# Revit family: Workstations-Multi_Level-Teknion-B_ASP_Secondary_Desk_for_Height_Adjustable_Peninsula-R2018
name_source: partatom
category: Furniture
revit_build: Autodesk Revit 2018 (Build: 20190510_1515(x64)
units: mm (PartAtom-declared; Revit-internal decimal feet)

## family parameters
Always vertical = Yes
Cut with Voids When Loaded = No
OmniClass Number = 23.40.20.00
OmniClass Title = General Furniture and Specialties
Room Calculation Point = No
Shared = Yes
Work Plane-Based = No

## types (5) — shared parameters
Assembly Code = E2020200
Manufacturer = Teknion
Manufacturer Fax = 416.661.4586
Part Number = B_ASP
Product Documentation Link = https://www.teknion.com
Product Line = Expansion Casegoods
Product Page URL = https://www.teknion.com
Series = Expansion Casegoods
Sustainability Data = https://www.teknion.com
URL = www.teknion.com
Unit Weight URL = http://www.teknion.com
Warranty = http://www.teknion.com

## per-type parameters (varying)
| type | Description | Height Adjustable Peninsula Depth | Model |
| 35" Height-Adjustable Peninsula Depth | Secondary Desk for Height-Adjustable Peninsula, 35" Height-Adjustable Peninsula Depth | 22.885 " | B_ASP_35________ |
| 41" Height-Adjustable Peninsula Depth | Secondary Desk for Height-Adjustable Peninsula, 41" Height-Adjustable Peninsula Depth | 28.855 " | B_ASP_41________ |
| 46" Height-Adjustable Peninsula Depth | Secondary Desk for Height-Adjustable Peninsula, 46" Height-Adjustable Peninsula Depth | 25.373 " | B_ASP_46________ |
| 52" Height-Adjustable Peninsula Depth | Secondary Desk for Height-Adjustable Peninsula, 52" Height-Adjustable Peninsula Depth | 31.343 " | B_ASP_52________ |
| 58" Height-Adjustable Peninsula Depth | Secondary Desk for Height-Adjustable Peninsula, 58" Height-Adjustable Peninsula Depth | 37.313 " | B_ASP_58________ |

## geometry (parser evidence)
native form markers: Sweep x4
no freeform markers — native parametric forms only
